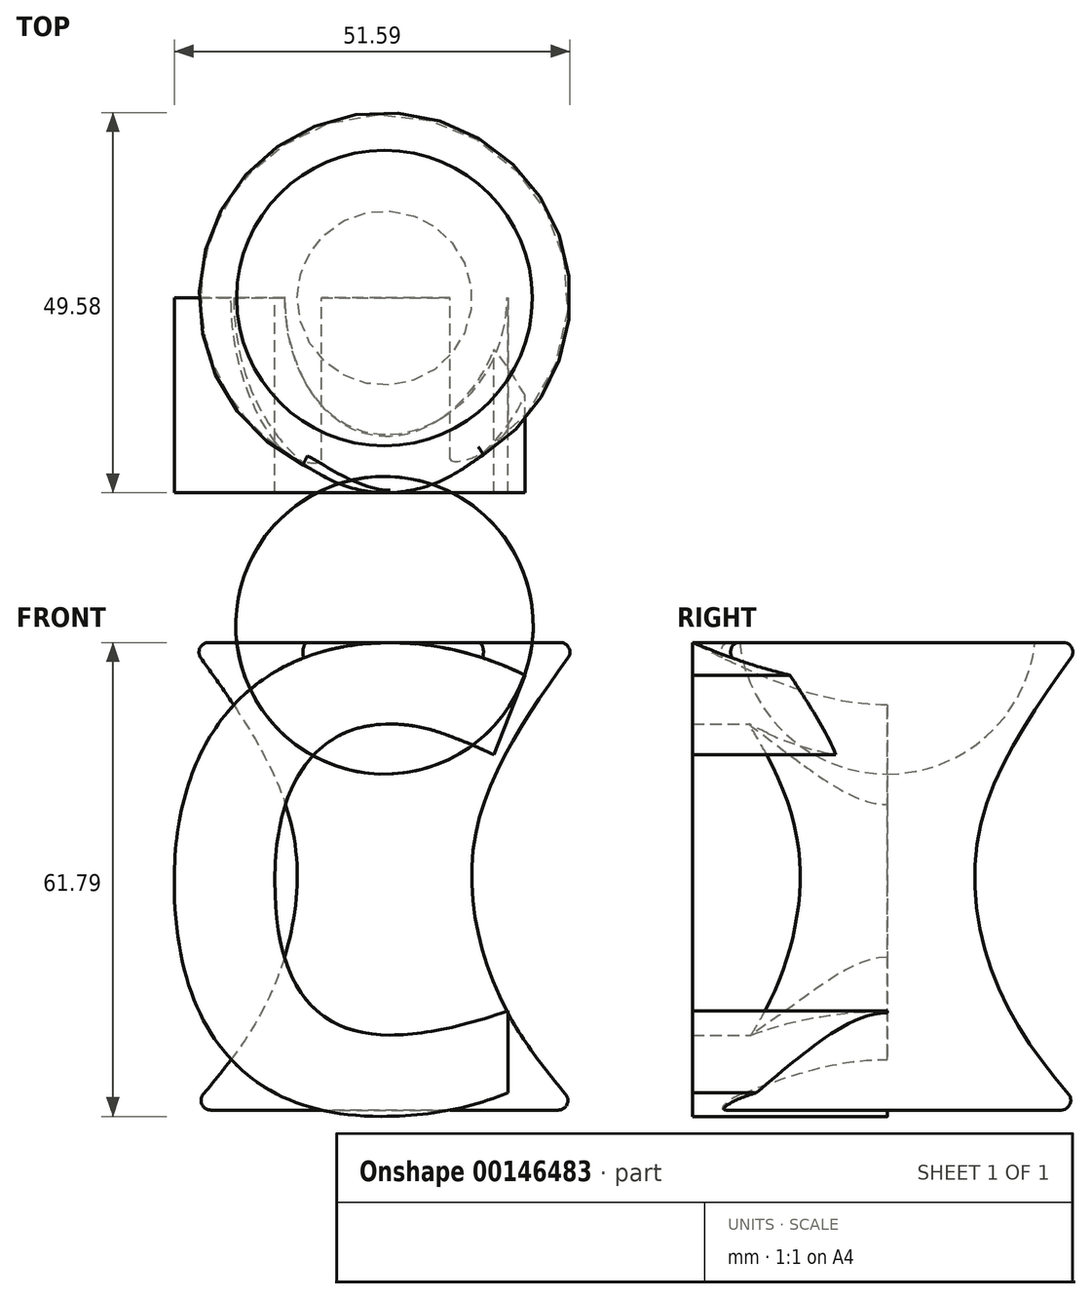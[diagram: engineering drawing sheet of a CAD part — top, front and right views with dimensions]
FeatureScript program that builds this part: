
annotation { "Feature Type Name" : "Feature", "Feature Type Description" : "" }
export const myFeature = defineFeature(function(context is Context, id is Id, definition is map)
    precondition{}
    {
        {
            var Q0;
            Q0=qCreatedBy(makeId("Top.planeOp"),FACE);
            var sketch = newSketch(context, id + "F0", { "sketchPlane" : qUnion([Q0])});
            skCircle(sketch, "E0", {"center": v(0, 0) * mm, "radius": 25.4 * mm});
            skSolve(sketch);
        }
        {
            var Q0;
            Q0 = qSketchRegion(id + "F0", true);
            extrude(context, id + "F1", {"entities" : qUnion([Q0]), "depth" : 60.96 * mm});
        }
        {
            var Q0;
            Q0=qCreatedBy(makeId("Front.planeOp"),FACE);
            var sketch = newSketch(context, id + "F2", { "sketchPlane" : qUnion([Q0])});
            skLineSegment(sketch, "E1", {"start": v(-25.4, 70.3) * mm, "end": v(-25.4, -27.32) * mm});
            skLineSegment(sketch, "E2", {"start": v(0, 71.27) * mm, "end": v(0, -29.26) * mm, "construction": true});
            skLineSegment(sketch, "E3", {"start": v(-67.02, 60.96) * mm, "end": v(48.08, 60.96) * mm, "construction": true});
            skFitSpline(sketch, "E4", {"points": [v(-25.4, 60.96) * mm, v(-11.9, 36.06) * mm, v(-15.3, 14.2) * mm, v(-25.4, 0) * mm], "startDerivative": vector(47.32, -65.24) * mm, "endDerivative": vector(-37.68, -43.9) * mm});
            skLineSegment(sketch, "E5", {"start": v(-25.4, 60.96) * mm, "end": v(-25.4, 0) * mm});
            skSolve(sketch);
        }
        {
            var Q0;
            Q0 = qSketchRegion(id + "F2", true);
            var Q1;
            Q1=sQuery(id+"F2.wireOp",EDGE,"E2");
            revolve(context, id + "F3", {"operationType" : NewBodyOperationType.REMOVE, "entities" : qUnion([Q0]), "axis" : qUnion([Q1]), "revolveType" : RevolveType.FULL, "oppositeDirection" : true});
        }
        {
            var Q0;
            Q0=qCreatedBy(makeId("Front.planeOp"),FACE);
            var sketch = newSketch(context, id + "F4", { "sketchPlane" : qUnion([Q0])});
            skText(sketch, "E6", { "text": "C", "fontName": "OpenSans-Bold.ttf"});
            const initialGuessF4  = {"E6": [-0.0323, 0, 1, 0, 0.06058]};
            skSetInitialGuess(sketch, initialGuessF4);
            skSolve(sketch);
        }
        {
            var Q0;
            Q0 = qSketchRegion(id + "F4", true);
            extrude(context, id + "F5", {"entities" : qUnion([Q0]), "operationType" : NewBodyOperationType.ADD, "depth" : 25.4 * mm});
        }
        {
            var Q0;
            Q0=qCreatedBy(makeId("Front.planeOp"),FACE);
            var sketch = newSketch(context, id + "F6", { "sketchPlane" : qUnion([Q0])});
            skArc(sketch, "E7", {"start": v(0, 82.6) * mm, "mid": v(-19.4, 63.2) * mm, "end": v(0, 43.8) * mm});
            skLineSegment(sketch, "E8", {"start": v(0, 82.6) * mm, "end": v(0, 43.8) * mm});
            skSolve(sketch);
        }
        {
            var Q0;
            Q0 = qSketchRegion(id + "F6", true);
            var Q1;
            Q1=sQuery(id+"F6.wireOp",EDGE,"E8");
            revolve(context, id + "F7", {"operationType" : NewBodyOperationType.REMOVE, "entities" : qUnion([Q0]), "axis" : qUnion([Q1]), "revolveType" : RevolveType.FULL, "oppositeDirection" : true});
        }
        {
            var Q0;
            {var subQ0=sQuery(id+"F2.wireOp",EDGE,"E5");var subQ1=sQuery(id+"F2.wireOp",EDGE,"E4");Q0=makeQuery(id+"F3.boolean.opBoolean","MERGE",EDGE,{"derivedFrom":[makeQuery(id+"F1.opExtrude","CAP_EDGE",EDGE,{"disambiguationData":[OSD([sQuery(id+"F0.wireOp",EDGE,"E0")])],"isStart":false}),makeQuery(id+"F3.opRevolve","SWEPT_EDGE",EDGE,{"disambiguationData":[OSD([subQ1,subQ0]),TDD([makeQuery(id+"F2.imprint","INTERSECT",VERTEX,{"disambiguationData":[OD(0.0)],"derivedFrom":[subQ1,subQ0]})])]})]});}
            var Q1;
            {var subQ0=sQuery(id+"F2.wireOp",EDGE,"E5");var subQ1=sQuery(id+"F2.wireOp",EDGE,"E4");Q1=makeQuery(id+"F3.boolean.opBoolean","MERGE",EDGE,{"derivedFrom":[makeQuery(id+"F1.opExtrude","CAP_EDGE",EDGE,{"disambiguationData":[OSD([sQuery(id+"F0.wireOp",EDGE,"E0")])],"isStart":true}),makeQuery(id+"F3.opRevolve","SWEPT_EDGE",EDGE,{"disambiguationData":[OSD([subQ1,subQ0]),TDD([makeQuery(id+"F2.imprint","INTERSECT",VERTEX,{"disambiguationData":[OD(1.0)],"derivedFrom":[subQ1,subQ0]})])]})]});}
            fillet(context, id + "F8", {"entities" : qUnion([Q0, Q1]), "radius" : 1.27 * mm, "tangentPropagation" : true, "allowEdgeOverflow" : false});
        }
    });
